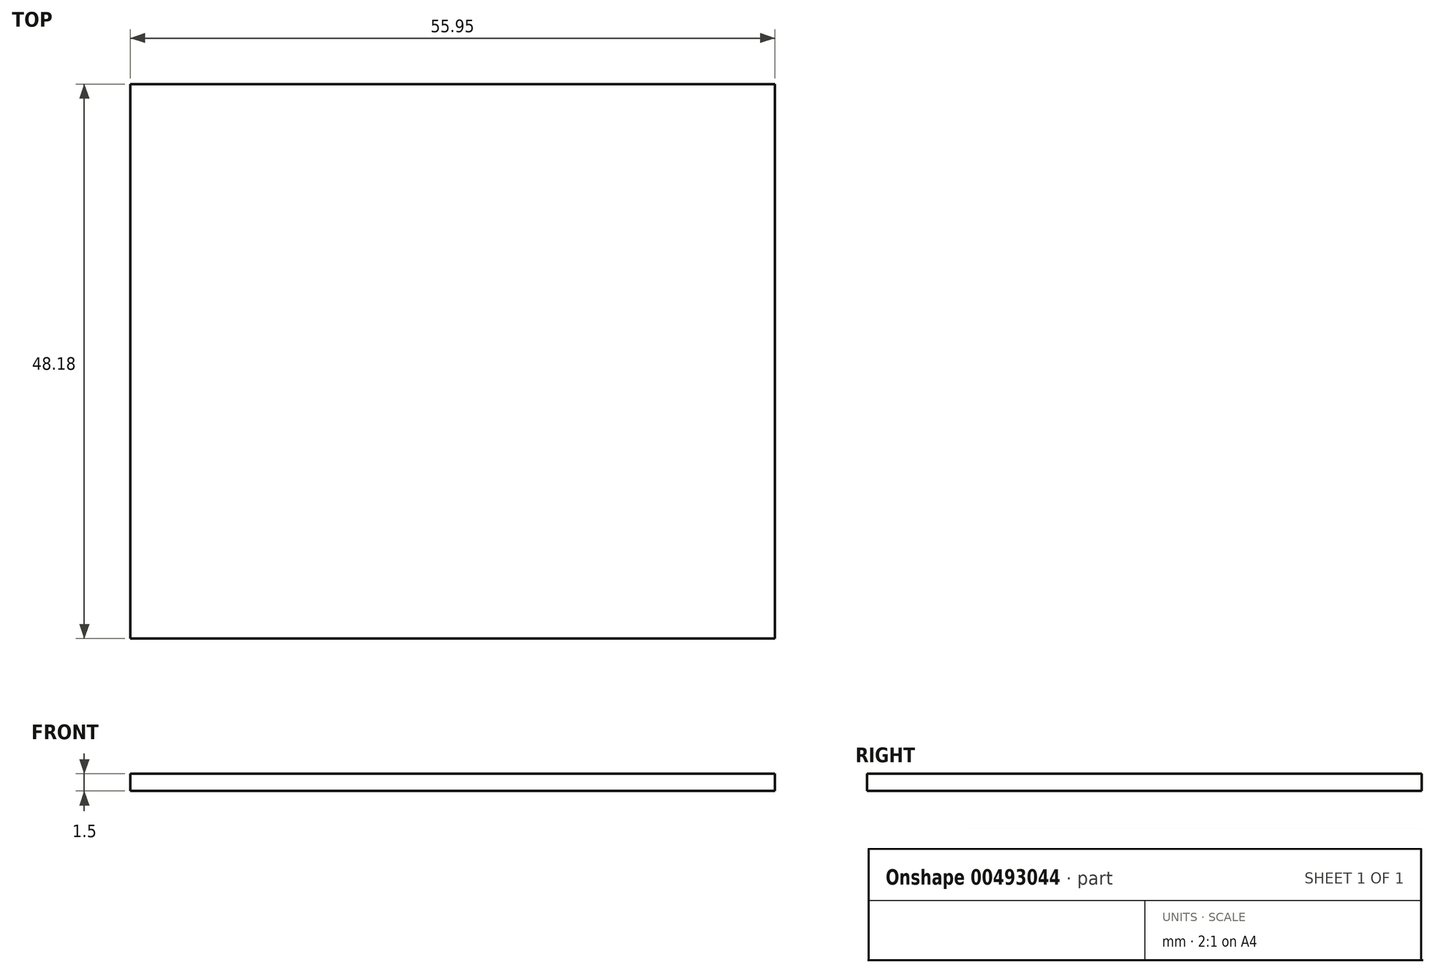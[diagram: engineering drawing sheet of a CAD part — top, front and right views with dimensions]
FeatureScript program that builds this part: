
annotation { "Feature Type Name" : "Feature", "Feature Type Description" : "" }
export const myFeature = defineFeature(function(context is Context, id is Id, definition is map)
    precondition{}
    {
        {
            var Q0;
            Q0=qCreatedBy(makeId("Top.planeOp"),FACE);
            var sketch = newSketch(context, id + "F0", { "sketchPlane" : qUnion([Q0])});
            skLineSegment(sketch, "E0.bottom", {"start": v(-30.17, -41.67) * mm, "end": v(25.78, -41.67) * mm});
            skLineSegment(sketch, "E0.top", {"start": v(-30.17, 6.5) * mm, "end": v(25.78, 6.5) * mm});
            skLineSegment(sketch, "E0.left", {"start": v(-30.17, -41.67) * mm, "end": v(-30.17, 6.5) * mm});
            skLineSegment(sketch, "E0.right", {"start": v(25.78, -41.67) * mm, "end": v(25.78, 6.5) * mm});
            skSolve(sketch);
        }
        {
            var Q0;
            Q0 = qSketchRegion(id + "F0", true);
            extrude(context, id + "F1", {"entities" : qUnion([Q0]), "depth" : 1.5 * mm});
        }
    });
